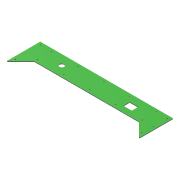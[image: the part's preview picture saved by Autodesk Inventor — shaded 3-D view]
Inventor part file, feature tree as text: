
AUTODESK INVENTOR PART (.ipt)
format: ipt  version: 2017 (Build 210142000, 142)  size: 823,296 bytes
history: native  units: mm
features: sketch x6, extrude x3, hole x1, projected_geometry x1
ambient origin geometry x8: Origin, YZ Plane, XZ Plane, XY Plane, X Axis, Y Axis, Z Axis, Center Point
bodies: Solid1 (feature_tree)
feature tree (11):
  extrude  "Extrusion1"  Depth=3.0mm TaperAngle=0.0deg
  sketch  "Sketch2"  dims[d6=5.0mm d7=6.0mm d8=4.0mm d9=2.0mm d10=90.0deg d11=8.0mm d12=20.594885mm d13=23.2mm]
  extrude  "Extrusion2"  Depth=23.2mm
  sketch  "Sketch5"
  hole  "Hole1"  [1 undecoded]
  extrude  "Extrusion3"  [1 undecoded]
  sketch  "Sketch8"
  sketch  "Sketch1"  dims[d0=3.0mm d1=0.0mm d4=194.0mm d5=0.0mm]
  projected_geometry  "Projected Loop1"
  sketch  "Sketch4"  dims[d14=10.0mm d15=0.0mm]
  sketch  "Sketch7"
note: 2 required parameter values undecoded (feature->parameter linkage not recoverable at this tier; creation-order binding heuristic only, values carry confidence <= 0.55)
